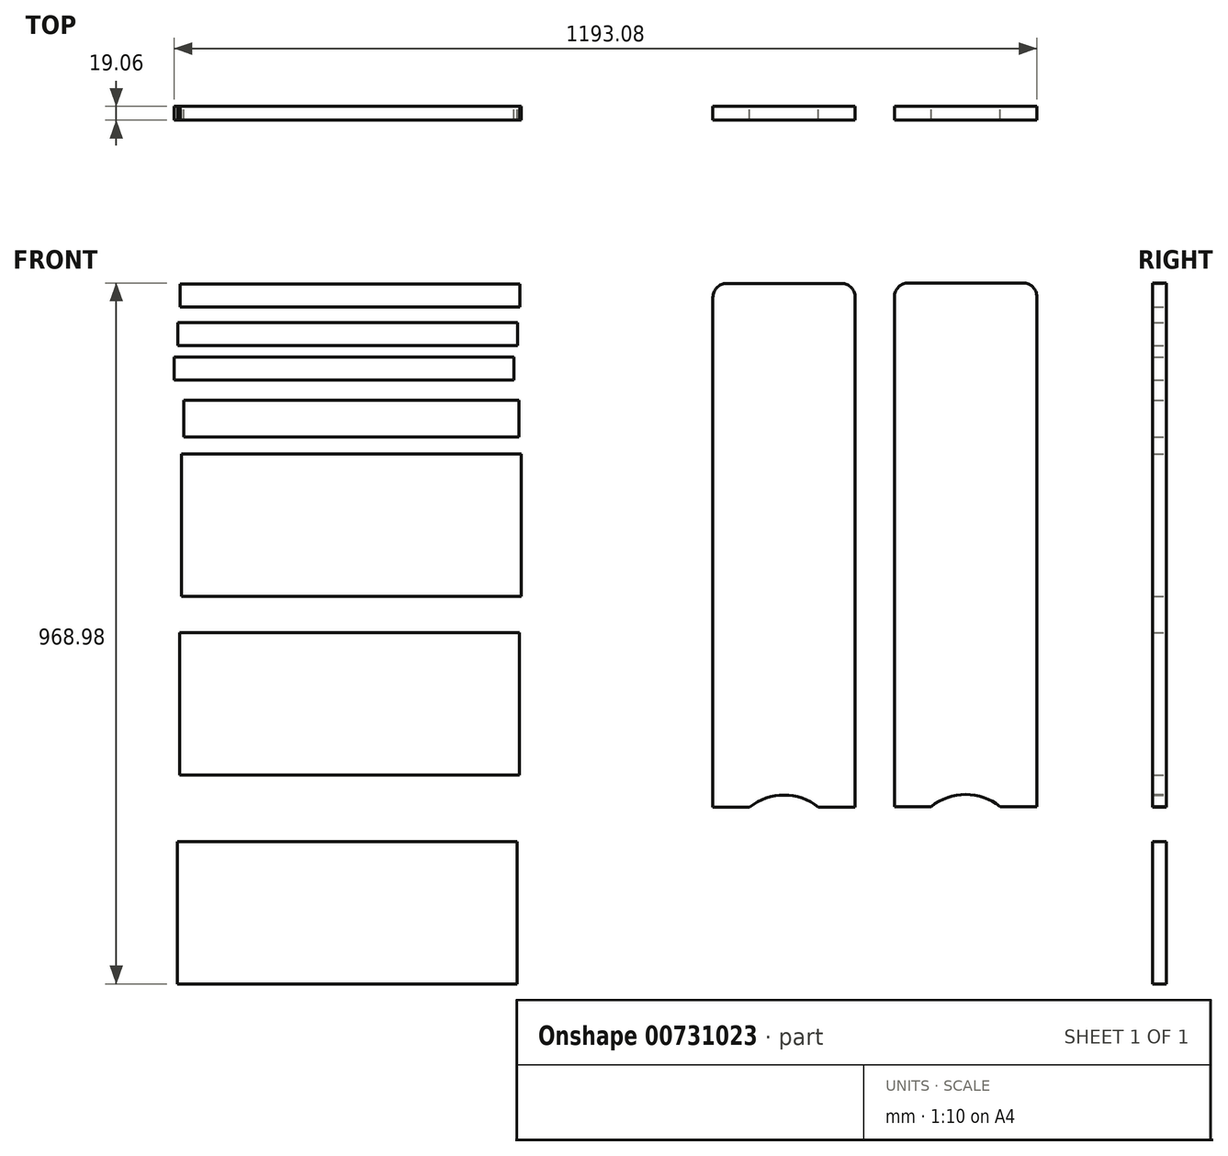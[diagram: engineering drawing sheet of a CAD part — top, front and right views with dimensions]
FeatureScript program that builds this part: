
annotation { "Feature Type Name" : "Feature", "Feature Type Description" : "" }
export const myFeature = defineFeature(function(context is Context, id is Id, definition is map)
    precondition{}
    {
        {
            var Q0;
            Q0=qCreatedBy(makeId("Front.planeOp"),FACE);
            var sketch = newSketch(context, id + "F0", { "sketchPlane" : qUnion([Q0])});
            skLineSegment(sketch, "E0.top", {"start": v(305.44, 361.95) * mm, "end": v(108.59, 361.95) * mm});
            skLineSegment(sketch, "E0.left", {"start": v(305.44, -361.95) * mm, "end": v(305.44, 361.95) * mm});
            skLineSegment(sketch, "E0.right", {"start": v(108.59, -361.95) * mm, "end": v(108.59, 361.95) * mm});
            skPoint(sketch, "E0.middle", {"position": v(207.01, 0) * mm});
            skLineSegment(sketch, "E1", {"start": v(108.59, -361.95) * mm, "end": v(159.39, -361.95) * mm});
            skLineSegment(sketch, "E2", {"start": v(305.44, -361.95) * mm, "end": v(254.64, -361.95) * mm});
            skArc(sketch, "E3", {"start": v(254.64, -361.95) * mm, "mid": v(207.01, -345.23) * mm, "end": v(159.39, -361.95) * mm});
            skSolve(sketch);
        }
        {
            var Q0;
            Q0=qCreatedBy(makeId("Front.planeOp"),FACE);
            var sketch = newSketch(context, id + "F1", { "sketchPlane" : qUnion([Q0])});
            skLineSegment(sketch, "E4.bottom", {"start": v(-156.6, -70.76) * mm, "end": v(-626.5, -70.76) * mm});
            skLineSegment(sketch, "E4.top", {"start": v(-156.6, 126.09) * mm, "end": v(-626.5, 126.09) * mm});
            skLineSegment(sketch, "E4.left", {"start": v(-156.6, -70.76) * mm, "end": v(-156.6, 126.09) * mm});
            skLineSegment(sketch, "E4.right", {"start": v(-626.5, -70.76) * mm, "end": v(-626.5, 126.09) * mm});
            skPoint(sketch, "E4.middle", {"position": v(-391.54, 27.66) * mm});
            skSolve(sketch);
        }
        {
            var Q0;
            Q0=qCreatedBy(makeId("Front.planeOp"),FACE);
            var sketch = newSketch(context, id + "F2", { "sketchPlane" : qUnion([Q0])});
            skLineSegment(sketch, "E5.bottom", {"start": v(-158.75, -317.5) * mm, "end": v(-628.65, -317.5) * mm});
            skLineSegment(sketch, "E5.top", {"start": v(-158.75, -120.65) * mm, "end": v(-628.65, -120.65) * mm});
            skLineSegment(sketch, "E5.left", {"start": v(-158.75, -317.5) * mm, "end": v(-158.75, -120.65) * mm});
            skLineSegment(sketch, "E5.right", {"start": v(-628.65, -317.5) * mm, "end": v(-628.65, -120.65) * mm});
            skPoint(sketch, "E5.middle", {"position": v(-393.7, -219.07) * mm});
            skSolve(sketch);
        }
        {
            var Q0;
            Q0=qCreatedBy(makeId("Front.planeOp"),FACE);
            var sketch = newSketch(context, id + "F3", { "sketchPlane" : qUnion([Q0])});
            skLineSegment(sketch, "E6.bottom", {"start": v(-162.38, -606.26) * mm, "end": v(-632.28, -606.26) * mm});
            skLineSegment(sketch, "E6.top", {"start": v(-162.38, -409.4) * mm, "end": v(-632.28, -409.4) * mm});
            skLineSegment(sketch, "E6.left", {"start": v(-162.38, -606.26) * mm, "end": v(-162.38, -409.4) * mm});
            skLineSegment(sketch, "E6.right", {"start": v(-632.28, -606.26) * mm, "end": v(-632.28, -409.4) * mm});
            skPoint(sketch, "E6.middle", {"position": v(-397.33, -507.83) * mm});
            skSolve(sketch);
        }
        {
            var Q0;
            Q0=qCreatedBy(makeId("Front.planeOp"),FACE);
            var sketch = newSketch(context, id + "F4", { "sketchPlane" : qUnion([Q0])});
            skLineSegment(sketch, "E7.bottom", {"start": v(-158.57, 329.33) * mm, "end": v(-628.47, 329.33) * mm});
            skLineSegment(sketch, "E7.top", {"start": v(-158.57, 361.08) * mm, "end": v(-628.47, 361.08) * mm});
            skLineSegment(sketch, "E7.left", {"start": v(-158.57, 329.33) * mm, "end": v(-158.57, 361.08) * mm});
            skLineSegment(sketch, "E7.right", {"start": v(-628.47, 329.33) * mm, "end": v(-628.47, 361.08) * mm});
            skPoint(sketch, "E7.middle", {"position": v(-393.52, 345.2) * mm});
            skSolve(sketch);
        }
        {
            var Q0;
            Q0=qCreatedBy(makeId("Front.planeOp"),FACE);
            var sketch = newSketch(context, id + "F5", { "sketchPlane" : qUnion([Q0])});
            skLineSegment(sketch, "E8.bottom", {"start": v(-159.6, 149.62) * mm, "end": v(-623.14, 149.62) * mm});
            skLineSegment(sketch, "E8.top", {"start": v(-159.6, 200.42) * mm, "end": v(-623.14, 200.42) * mm});
            skLineSegment(sketch, "E8.left", {"start": v(-159.6, 149.62) * mm, "end": v(-159.6, 200.42) * mm});
            skLineSegment(sketch, "E8.right", {"start": v(-623.14, 149.62) * mm, "end": v(-623.14, 200.42) * mm});
            skPoint(sketch, "E8.middle", {"position": v(-391.37, 175.02) * mm});
            skSolve(sketch);
        }
        {
            var Q0;
            Q0=qCreatedBy(makeId("Front.planeOp"),FACE);
            var sketch = newSketch(context, id + "F6", { "sketchPlane" : qUnion([Q0])});
            skLineSegment(sketch, "E9.bottom", {"start": v(-161.89, 276.17) * mm, "end": v(-631.79, 276.17) * mm});
            skLineSegment(sketch, "E9.top", {"start": v(-161.89, 307.92) * mm, "end": v(-631.79, 307.92) * mm});
            skLineSegment(sketch, "E9.left", {"start": v(-161.89, 276.17) * mm, "end": v(-161.89, 307.92) * mm});
            skLineSegment(sketch, "E9.right", {"start": v(-631.79, 276.17) * mm, "end": v(-631.79, 307.92) * mm});
            skPoint(sketch, "E9.middle", {"position": v(-396.84, 292.04) * mm});
            skSolve(sketch);
        }
        {
            var Q0;
            Q0=qCreatedBy(makeId("Front.planeOp"),FACE);
            var sketch = newSketch(context, id + "F7", { "sketchPlane" : qUnion([Q0])});
            skLineSegment(sketch, "E10.bottom", {"start": v(-166.65, 228.27) * mm, "end": v(-636.55, 228.27) * mm});
            skLineSegment(sketch, "E10.top", {"start": v(-166.65, 260.02) * mm, "end": v(-636.55, 260.02) * mm});
            skLineSegment(sketch, "E10.left", {"start": v(-166.65, 228.27) * mm, "end": v(-166.65, 260.02) * mm});
            skLineSegment(sketch, "E10.right", {"start": v(-636.55, 228.27) * mm, "end": v(-636.55, 260.02) * mm});
            skPoint(sketch, "E10.middle", {"position": v(-401.6, 244.14) * mm});
            skSolve(sketch);
        }
        {
            var Q0;
            Q0=qCreatedBy(makeId("Front.planeOp"),FACE);
            var sketch = newSketch(context, id + "F8", { "sketchPlane" : qUnion([Q0])});
            skLineSegment(sketch, "E11.top", {"start": v(556.53, 362.72) * mm, "end": v(359.68, 362.72) * mm});
            skLineSegment(sketch, "E11.left", {"start": v(556.53, -361.18) * mm, "end": v(556.53, 362.72) * mm});
            skLineSegment(sketch, "E11.right", {"start": v(359.68, -361.18) * mm, "end": v(359.68, 362.72) * mm});
            skPoint(sketch, "E11.middle", {"position": v(458.1, 0.77) * mm});
            skLineSegment(sketch, "E12", {"start": v(359.68, -361.18) * mm, "end": v(410.48, -361.18) * mm});
            skLineSegment(sketch, "E13", {"start": v(556.53, -361.18) * mm, "end": v(505.73, -361.18) * mm});
            skArc(sketch, "E14", {"start": v(505.73, -361.18) * mm, "mid": v(458.1, -344.47) * mm, "end": v(410.48, -361.18) * mm});
            skSolve(sketch);
        }
        {
            var Q0;
            Q0 = qSketchRegion(id + "F8", true);
            var Q1;
            Q1=makeQuery(id+"F4.imprint","IMPRINT",FACE,{"disambiguationData":[TD([[makeQuery(id+"F4.imprint","IMPRINT",EDGE,{"derivedFrom":sQuery(id+"F4.wireOp",EDGE,"E7.bottom")}),-1.0]])]});
            var Q2;
            Q2=makeQuery(id+"F6.imprint","IMPRINT",FACE,{"disambiguationData":[TD([[makeQuery(id+"F6.imprint","IMPRINT",EDGE,{"derivedFrom":sQuery(id+"F6.wireOp",EDGE,"E9.bottom")}),-1.0]])]});
            var Q3;
            Q3=makeQuery(id+"F7.imprint","IMPRINT",FACE,{"disambiguationData":[TD([[makeQuery(id+"F7.imprint","IMPRINT",EDGE,{"derivedFrom":sQuery(id+"F7.wireOp",EDGE,"E10.bottom")}),-1.0]])]});
            var Q4;
            Q4=makeQuery(id+"F5.imprint","IMPRINT",FACE,{"disambiguationData":[TD([[makeQuery(id+"F5.imprint","IMPRINT",EDGE,{"derivedFrom":sQuery(id+"F5.wireOp",EDGE,"E8.bottom")}),-1.0]])]});
            var Q5;
            Q5=makeQuery(id+"F1.imprint","IMPRINT",FACE,{"disambiguationData":[TD([[makeQuery(id+"F1.imprint","IMPRINT",EDGE,{"derivedFrom":sQuery(id+"F1.wireOp",EDGE,"E4.bottom")}),-1.0]])]});
            var Q6;
            Q6=makeQuery(id+"F2.imprint","IMPRINT",FACE,{"disambiguationData":[TD([[makeQuery(id+"F2.imprint","IMPRINT",EDGE,{"derivedFrom":sQuery(id+"F2.wireOp",EDGE,"E5.bottom")}),-1.0]])]});
            var Q7;
            Q7=makeQuery(id+"F3.imprint","IMPRINT",FACE,{"disambiguationData":[TD([[makeQuery(id+"F3.imprint","IMPRINT",EDGE,{"derivedFrom":sQuery(id+"F3.wireOp",EDGE,"E6.bottom")}),-1.0]])]});
            var Q8;
            Q8=makeQuery(id+"F0.imprint","IMPRINT",FACE,{"disambiguationData":[TD([[makeQuery(id+"F0.imprint","IMPRINT",EDGE,{"derivedFrom":sQuery(id+"F0.wireOp",EDGE,"E0.top")}),1.0]])]});
            extrude(context, id + "F9", {"entities" : qUnion([Q0, Q1, Q2, Q3, Q4, Q5, Q6, Q7, Q8]), "endBound" : BoundingType.SYMMETRIC, "depth" : 19.05 * mm, "offsetDistance" : 25.4 * mm});
        }
        {
            var Q0;
            Q0=makeQuery(id+"F9.opExtrude","SWEPT_EDGE",EDGE,{"disambiguationData":[OSD([sQuery(id+"F0.wireOp",EDGE,"E0.top"),sQuery(id+"F0.wireOp",EDGE,"E0.right")])]});
            var Q1;
            Q1=makeQuery(id+"F9.opExtrude","SWEPT_EDGE",EDGE,{"disambiguationData":[OSD([sQuery(id+"F0.wireOp",EDGE,"E0.top"),sQuery(id+"F0.wireOp",EDGE,"E0.left")])]});
            var Q2;
            Q2=makeQuery(id+"F9.opExtrude","SWEPT_EDGE",EDGE,{"disambiguationData":[OSD([sQuery(id+"F8.wireOp",EDGE,"E11.top"),sQuery(id+"F8.wireOp",EDGE,"E11.right")])]});
            var Q3;
            Q3=makeQuery(id+"F9.opExtrude","SWEPT_EDGE",EDGE,{"disambiguationData":[OSD([sQuery(id+"F8.wireOp",EDGE,"E11.top"),sQuery(id+"F8.wireOp",EDGE,"E11.left")])]});
            fillet(context, id + "F10", {"entities" : qUnion([Q0, Q1, Q2, Q3]), "radius" : 19.05 * mm, "tangentPropagation" : true, "allowEdgeOverflow" : false});
        }
    });
